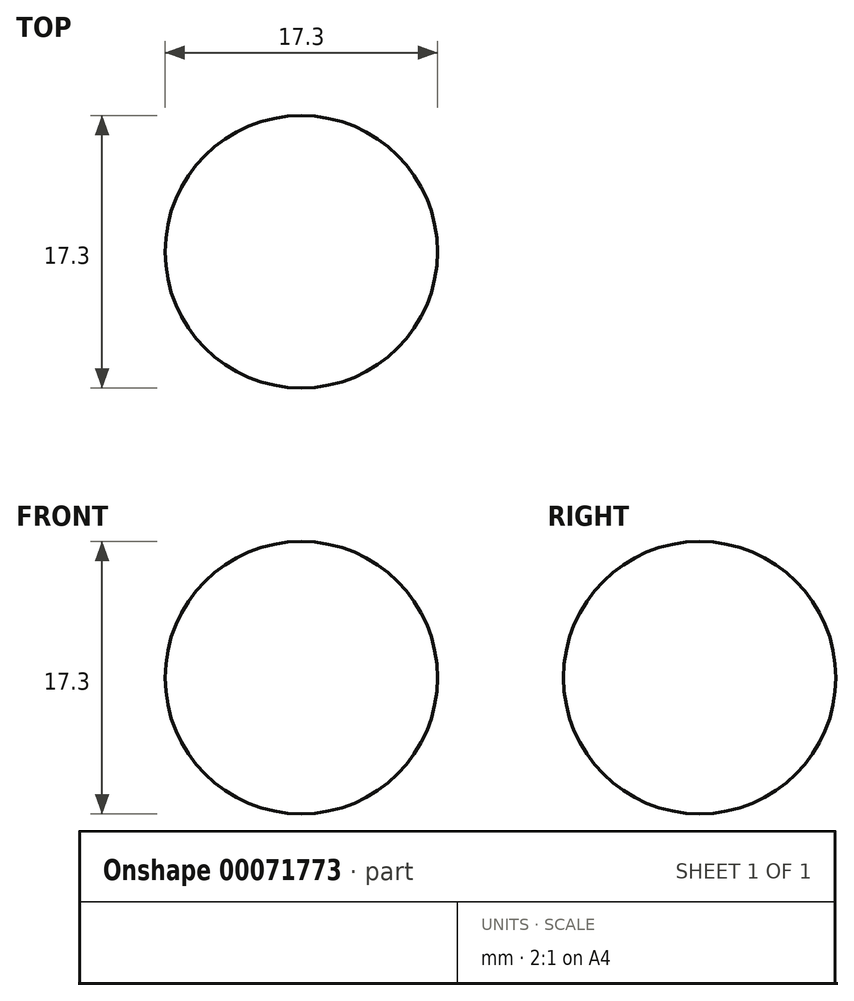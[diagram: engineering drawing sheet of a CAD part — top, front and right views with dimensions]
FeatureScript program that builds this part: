
annotation { "Feature Type Name" : "Feature", "Feature Type Description" : "" }
export const myFeature = defineFeature(function(context is Context, id is Id, definition is map)
    precondition{}
    {
        {
            var Q0;
            Q0=qCreatedBy(makeId("Front.planeOp"),FACE);
            var sketch = newSketch(context, id + "F0", { "sketchPlane" : qUnion([Q0])});
            skCircle(sketch, "E0", {"center": v(0, 0) * mm, "radius": 8.65 * mm});
            skLineSegment(sketch, "E1", {"start": v(0, 8.65) * mm, "end": v(0, -8.65) * mm});
            skSolve(sketch);
        }
        {
            var Q0;
            {var subQ0=sQuery(id+"F0.wireOp",EDGE,"E1");Q0=makeQuery(id+"F0.imprint","IMPRINT",FACE,{"disambiguationData":[TD([[makeQuery(id+"F0.imprint","IMPRINT",EDGE,{"derivedFrom":subQ0}),-1.0]])]});}
            var Q1;
            Q1=sQuery(id+"F0.wireOp",EDGE,"E1");
            revolve(context, id + "F1", {"entities" : qUnion([Q0]), "axis" : qUnion([Q1]), "revolveType" : RevolveType.FULL});
        }
    });
